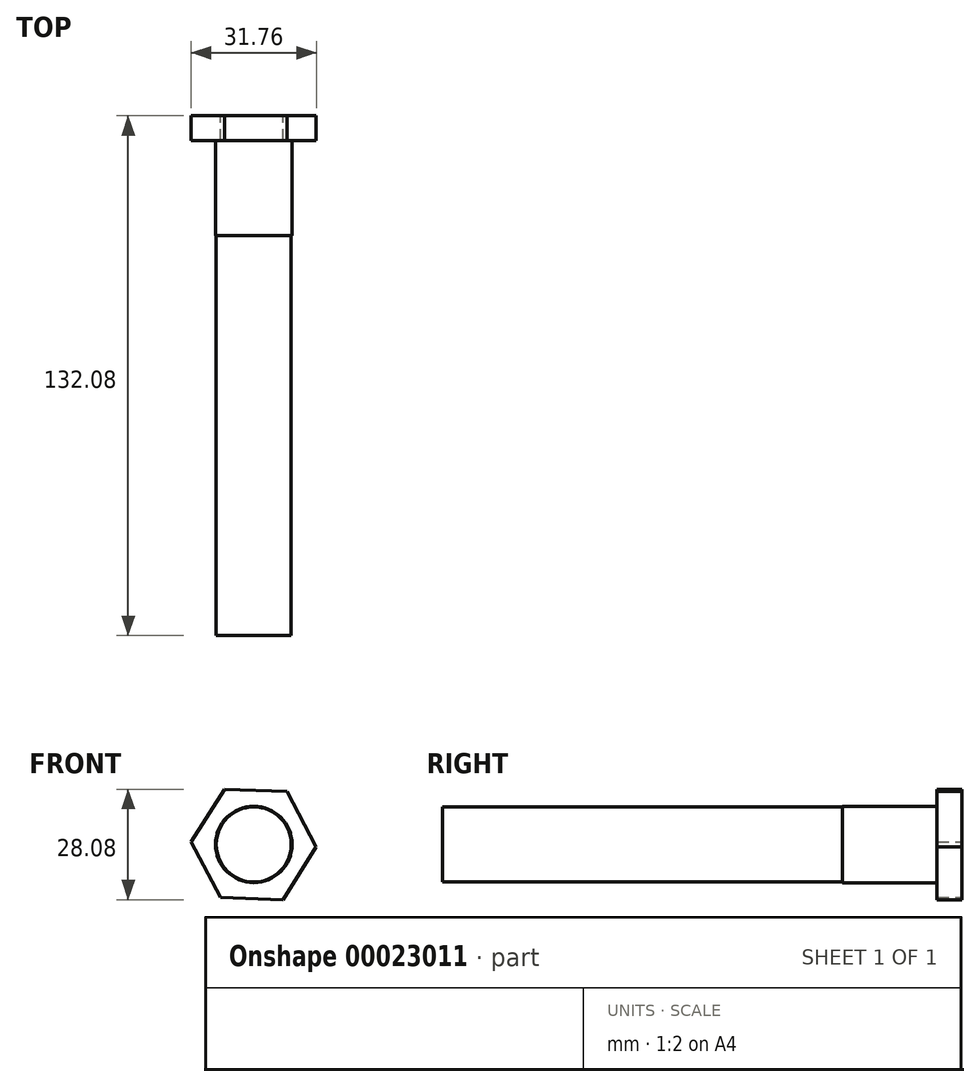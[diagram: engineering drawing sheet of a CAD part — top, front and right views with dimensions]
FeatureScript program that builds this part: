
annotation { "Feature Type Name" : "Feature", "Feature Type Description" : "" }
export const myFeature = defineFeature(function(context is Context, id is Id, definition is map)
    precondition{}
    {
        {
            var Q0;
            Q0=qCreatedBy(makeId("Front.planeOp"),FACE);
            var sketch = newSketch(context, id + "F0", { "sketchPlane" : qUnion([Q0])});
            skCircle(sketch, "E0", {"center": v(0, 0) * mm, "radius": 9.53 * mm});
            skSolve(sketch);
        }
        {
            var Q0;
            Q0 = qSketchRegion(id + "F0", true);
            extrude(context, id + "F1", {"entities" : qUnion([Q0]), "depth" : 101.6 * mm});
        }
        {
            var Q0;
            Q0=qCreatedBy(makeId("Front.planeOp"),FACE);
            var sketch = newSketch(context, id + "F2", { "sketchPlane" : qUnion([Q0])});
            skCircle(sketch, "E1.cCircle", {"center": v(0, 0) * mm, "radius": 13.76 * mm, "construction": true});
            skLineSegment(sketch, "E1.0", {"start": v(15.88, -0.59) * mm, "end": v(7.43, -14.04) * mm});
            skLineSegment(sketch, "E1.1", {"start": v(7.43, -14.04) * mm, "end": v(-8.45, -13.46) * mm});
            skLineSegment(sketch, "E1.2", {"start": v(-8.45, -13.46) * mm, "end": v(-15.88, 0.59) * mm});
            skLineSegment(sketch, "E1.3", {"start": v(-15.88, 0.59) * mm, "end": v(-7.43, 14.04) * mm});
            skLineSegment(sketch, "E1.4", {"start": v(-7.43, 14.04) * mm, "end": v(8.45, 13.46) * mm});
            skLineSegment(sketch, "E1.5", {"start": v(8.45, 13.46) * mm, "end": v(15.88, -0.59) * mm});
            skPoint(sketch, "E1.0.midPoint", {"position": v(11.65, -7.31) * mm});
            skSolve(sketch);
        }
        {
            var Q0;
            Q0 = qSketchRegion(id + "F2", true);
            extrude(context, id + "F3", {"entities" : qUnion([Q0]), "operationType" : NewBodyOperationType.ADD, "depth" : 6.35 * mm});
        }
        {
            var Q0;
            Q0=qCreatedBy(makeId("Front.planeOp"),FACE);
            var sketch = newSketch(context, id + "F4", { "sketchPlane" : qUnion([Q0])});
            skCircle(sketch, "E2", {"center": v(0, 0) * mm, "radius": 9.71 * mm});
            skSolve(sketch);
        }
        {
            var Q0;
            Q0 = qSketchRegion(id + "F4", true);
            var Q1;
            Q1=makeQuery(id+"F1.opExtrude","CAP_FACE",FACE,{"disambiguationData":[OSD([sQuery(id+"F0.wireOp",EDGE,"E0")])],"isStart":false});
            extrude(context, id + "F5", {"entities" : qUnion([Q0, Q1]), "operationType" : NewBodyOperationType.ADD, "depth" : 30.48 * mm});
        }
    });
